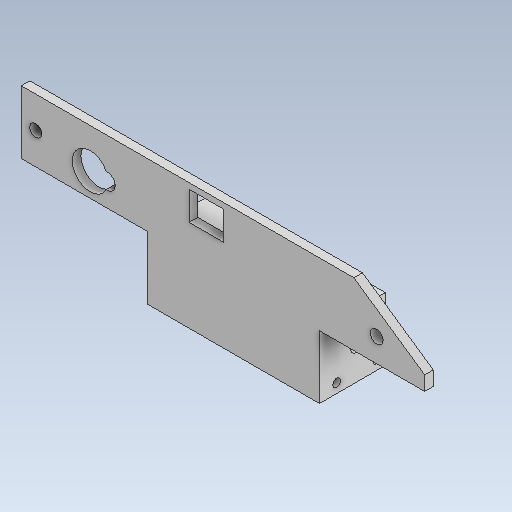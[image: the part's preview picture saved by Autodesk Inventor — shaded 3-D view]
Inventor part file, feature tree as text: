
AUTODESK INVENTOR PART (.ipt)
format: ipt  version: 2020 (Build 240168000, 168)  size: 222,720 bytes
history: native  units: mm
features: reference x28, other x8, sketch x6, extrude x5, hole x3
ambient origin geometry x8: Origin, YZ Plane, XZ Plane, XY Plane, X Axis, Y Axis, Z Axis, Center Point
bodies: Body1 (feature_tree)
feature tree (50):
  other  "Bryła1"
  extrude  "Wyciągnięcie proste1"  Depth=0.25mm
  extrude  "Wyciągnięcie proste2"  Depth=12.5mm
  sketch  "Szkic4"
  hole  "Otwór2"  [1 undecoded]
  extrude  "Wyciągnięcie proste3"  Depth=2.0mm
  extrude  "Wyciągnięcie proste4"  Depth=10.0mm
  hole  "Otwór3"  [1 undecoded]
  extrude  "Wyciągnięcie proste5"  Depth=10.0mm
  hole  "Otwór1"  [1 undecoded]
  reference  "Odniesienie1"
  reference  "Odniesienie2"
  reference  "Odniesienie3"
  reference  "Odniesienie4"
  reference  "Odniesienie5"
  reference  "Odniesienie6"
  reference  "Odniesienie7"
  reference  "Odniesienie8"
  reference  "Odniesienie9"
  reference  "Odniesienie10"
  reference  "Odniesienie11"
  reference  "Odniesienie12"
  reference  "Odniesienie13"
  sketch  "Szkic2"
  sketch  "Szkic5"
  reference  "Odniesienie14"
  reference  "Odniesienie15"
  reference  "Odniesienie16"
  reference  "Odniesienie17"
  reference  "Odniesienie18"
  reference  "Odniesienie19"
  reference  "Odniesienie20"
  reference  "Odniesienie21"
  reference  "Odniesienie22"
  reference  "Odniesienie23"
  reference  "Odniesienie24"
  reference  "Odniesienie25"
  sketch  "Szkic6"
  sketch  "Szkic7"
  reference  "Odniesienie26"
  reference  "Odniesienie27"
  reference  "Odniesienie28"
  sketch  "Szkic8"
  other  "<userpath>\Desktop\3d\scanning-robot\Assembly1.iam"
  other  "Assembly1.iam"
  other  "base:1"
  other  "Tower Pro MG90S Micro servo:2"
  other  "Крышка корпуса:1"
  other  "AS 1112 (2) - Metryczny M4  Typ 5:1"
  other  "coupler:1"
note: 3 required parameter values undecoded (feature->parameter linkage not recoverable at this tier; creation-order binding heuristic only, values carry confidence <= 0.55)
